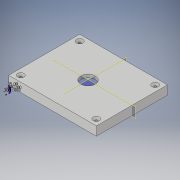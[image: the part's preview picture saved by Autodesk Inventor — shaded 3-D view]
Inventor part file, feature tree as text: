
AUTODESK INVENTOR PART (.ipt)
format: ipt  version: 2019 (Build 230136000, 136)  size: 156,672 bytes
history: native  units: in
note: dims shown in document units (in); Inventor stores cm internally (conversion verified against a paired STEP export)
features: sketch x5, extrude x4, plane x2, mirror x2, chamfer x1
ambient origin geometry x8: Origin, YZ Plane, XZ Plane, XY Plane, X Axis, Y Axis, Z Axis, Center Point
bodies: Solid1 (feature_tree)
feature tree (14):
  extrude  "Extrusion1"  Depth=2.808in
  extrude  "Extrusion2"  Depth=0.14in
  extrude  "Extrusion3"  Depth=0.14in
  sketch  "Sketch5"  dims[d6=0.25in d7=0.0in d8=3.088in]
  extrude  "Extrusion6"  Depth=3.088in
  chamfer  "Chamfer1"  Distance=0.14in
  plane  "Work Plane4"
  plane  "Work Plane5"
  mirror  "Mirror3"
  mirror  "Mirror4"
  sketch  "Sketch1"  dims[d0=3.535in d1=2.808in]
  sketch  "Sketch2"  dims[d2=0.14in d3=0.14in]
  sketch  "Sketch3"  dims[d4=0.14in d5=0.14in]
  sketch  "Sketch7"  dims[d9=3.815in d10=0.14in d11=0.0in d12=1.9075in d13=1.544in d14=0.631in d15=0.14in d16=0.04in d17=0.0in d18=0.0in d19=0.05in d20=0.3in d21=0.2405in d22=0.2in d23=0.03in d40=0.1065in d41=0.2465in d42=1.0in d43=0.0in d44=0.075in d45=0.125in d46=0.3367in d47=-1.9075in d48=-1.544in]
